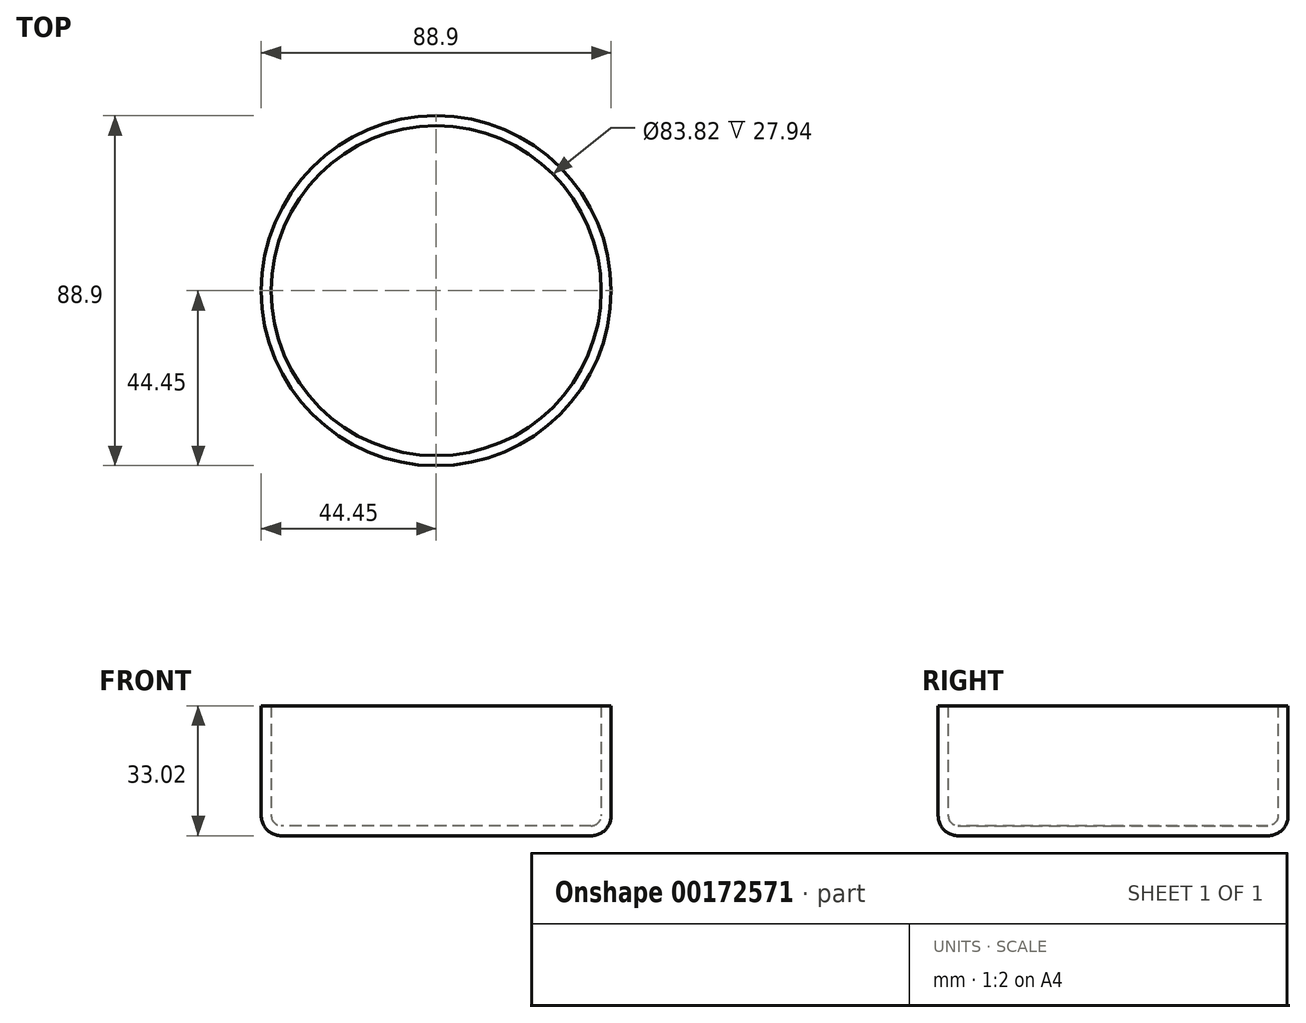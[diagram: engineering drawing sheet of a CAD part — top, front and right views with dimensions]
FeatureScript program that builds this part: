
annotation { "Feature Type Name" : "Feature", "Feature Type Description" : "" }
export const myFeature = defineFeature(function(context is Context, id is Id, definition is map)
    precondition{}
    {
        {
            var Q0;
            Q0=qCreatedBy(makeId("Top.planeOp"),FACE);
            var sketch = newSketch(context, id + "F0", { "sketchPlane" : qUnion([Q0])});
            skCircle(sketch, "E0", {"center": v(-20.76, -22.06) * mm, "radius": 44.45 * mm});
            skSolve(sketch);
        }
        {
            var Q0;
            Q0 = qSketchRegion(id + "F0", true);
            extrude(context, id + "F1", {"entities" : qUnion([Q0]), "depth" : 38.1 * mm});
        }
        {
            var Q0;
            Q0=makeQuery(id+"F1.opExtrude","CAP_FACE",FACE,{"disambiguationData":[OSD([sQuery(id+"F0.wireOp",EDGE,"E0")])],"isStart":false});
            var Q1;
            Q1=makeQuery(id+"F1.opExtrude","SWEPT_FACE",FACE,{"disambiguationData":[OSD([sQuery(id+"F0.wireOp",EDGE,"E0")])]});
            fillet(context, id + "F2", {"entities" : qUnion([Q0, Q1]), "radius" : 5.08 * mm, "tangentPropagation" : true, "allowEdgeOverflow" : false});
        }
        {
            var Q0;
            Q0=makeQuery(id+"F1.opExtrude","CAP_FACE",FACE,{"disambiguationData":[OSD([sQuery(id+"F0.wireOp",EDGE,"E0")])],"isStart":false});
            var Q1;
            {var subQ0=sQuery(id+"F0.wireOp",EDGE,"E0");Q1=makeQuery(id+"F2.opFillet","BLEND_FACE",FACE,{"disambiguationData":[OSD([subQ0]),TDD([makeQuery(id+"F1.opExtrude","CAP_EDGE",EDGE,{"disambiguationData":[OSD([subQ0])],"isStart":false})])]});}
            shell(context, id + "F3", {"entities" : qUnion([Q0, Q1]), "thickness" : 2.54 * mm});
        }
    });
